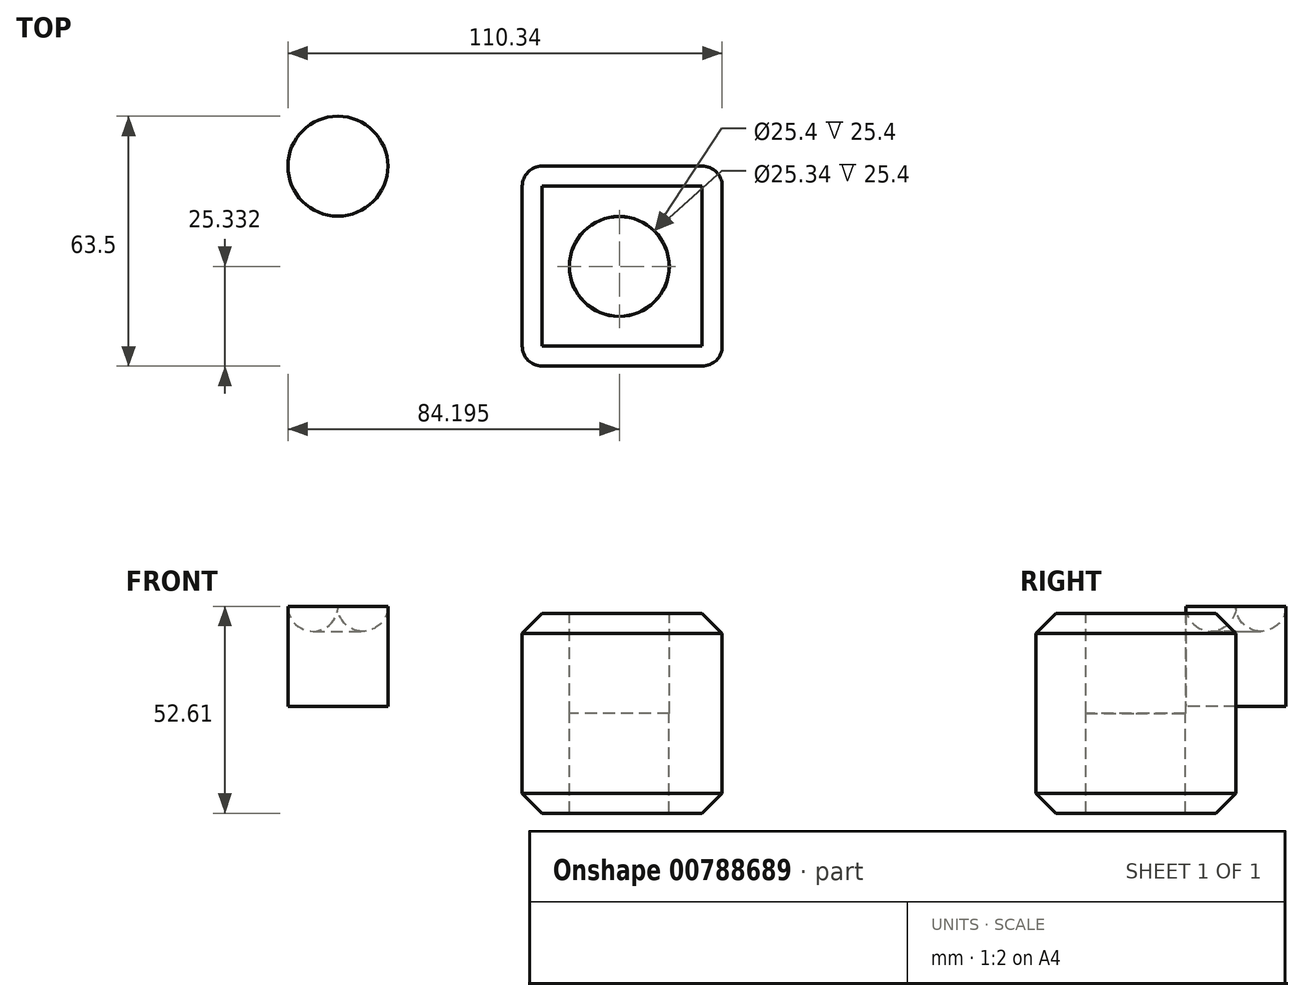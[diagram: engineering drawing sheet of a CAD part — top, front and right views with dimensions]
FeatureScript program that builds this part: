
annotation { "Feature Type Name" : "Feature", "Feature Type Description" : "" }
export const myFeature = defineFeature(function(context is Context, id is Id, definition is map)
    precondition{}
    {
        {
            var Q0;
            Q0=qCreatedBy(makeId("Front.planeOp"),FACE);
            var sketch = newSketch(context, id + "F0", { "sketchPlane" : qUnion([Q0])});
            skLineSegment(sketch, "E0", {"start": v(-40.12, 34.82) * mm, "end": v(-40.12, 9.42) * mm});
            skLineSegment(sketch, "E1", {"start": v(-40.12, 9.42) * mm, "end": v(-27.42, 9.42) * mm});
            skLineSegment(sketch, "E2", {"start": v(-27.42, 9.42) * mm, "end": v(-27.42, 35.24) * mm});
            skArc(sketch, "E3", {"start": v(-27.42, 35.24) * mm, "mid": v(-33.97, 41.17) * mm, "end": v(-40.12, 34.82) * mm});
            skSolve(sketch);
        }
        {
            var Q0;
            Q0 = qSketchRegion(id + "F0", true);
            var Q1;
            Q1=sQuery(id+"F0.wireOp",EDGE,"E2");
            revolve(context, id + "F1", {"surfaceOperationType" : NewSurfaceOperationType.NEW, "entities" : qUnion([Q0]), "axis" : qUnion([Q1]), "revolveType" : RevolveType.FULL});
        }
        {
            var Q0;
            Q0=qCreatedBy(makeId("Front.planeOp"),FACE);
            var sketch = newSketch(context, id + "F2", { "sketchPlane" : qUnion([Q0])});
            skLineSegment(sketch, "E4", {"start": v(19.42, 33) * mm, "end": v(19.42, -17.8) * mm});
            skLineSegment(sketch, "E5", {"start": v(19.42, -17.8) * mm, "end": v(70.22, -17.8) * mm});
            skLineSegment(sketch, "E6", {"start": v(70.22, -17.8) * mm, "end": v(70.22, 33) * mm});
            skLineSegment(sketch, "E7", {"start": v(70.22, 33) * mm, "end": v(19.42, 33) * mm});
            skSolve(sketch);
        }
        {
            var Q0;
            Q0 = qSketchRegion(id + "F2", true);
            extrude(context, id + "F3", {"entities" : qUnion([Q0]), "depth" : 50.8 * mm, "offsetDistance" : 25.4 * mm});
        }
        {
            var Q0;
            Q0=makeQuery(id+"F3.opExtrude","CAP_EDGE",EDGE,{"disambiguationData":[OSD([sQuery(id+"F2.wireOp",EDGE,"E4")])],"isStart":false});
            fillet(context, id + "F4", {"entities" : qUnion([Q0]), "radius" : 5.08 * mm, "tangentPropagation" : true, "allowEdgeOverflow" : false});
        }
        {
            var Q0;
            Q0=makeQuery(id+"F3.opExtrude","CAP_EDGE",EDGE,{"disambiguationData":[OSD([sQuery(id+"F2.wireOp",EDGE,"E6")])],"isStart":false});
            var Q1;
            Q1=makeQuery(id+"F3.opExtrude","CAP_EDGE",EDGE,{"disambiguationData":[OSD([sQuery(id+"F2.wireOp",EDGE,"E6")])],"isStart":true});
            fillet(context, id + "F5", {"entities" : qUnion([Q0, Q1]), "radius" : 5.08 * mm, "tangentPropagation" : true, "allowEdgeOverflow" : false});
        }
        {
            var Q0;
            Q0=makeQuery(id+"F3.opExtrude","CAP_EDGE",EDGE,{"disambiguationData":[OSD([sQuery(id+"F2.wireOp",EDGE,"E4")])],"isStart":true});
            fillet(context, id + "F6", {"entities" : qUnion([Q0]), "radius" : 5.08 * mm, "tangentPropagation" : true, "allowEdgeOverflow" : false});
        }
        {
            var Q0;
            Q0=makeQuery(id+"F3.opExtrude","SWEPT_FACE",FACE,{"disambiguationData":[OSD([sQuery(id+"F2.wireOp",EDGE,"E7")])]});
            chamfer(context, id + "F7", {"entities" : qUnion([Q0]), "width" : 5.08 * mm, "tangentPropagation" : true});
        }
        {
            var Q0;
            Q0=makeQuery(id+"F3.opExtrude","SWEPT_FACE",FACE,{"disambiguationData":[OSD([sQuery(id+"F2.wireOp",EDGE,"E5")])]});
            chamfer(context, id + "F8", {"entities" : qUnion([Q0]), "width" : 5.08 * mm, "tangentPropagation" : true});
        }
        {
            var Q0;
            Q0=makeQuery(id+"F3.opExtrude","SWEPT_FACE",FACE,{"disambiguationData":[OSD([sQuery(id+"F2.wireOp",EDGE,"E7")])]});
            var sketch = newSketch(context, id + "F9", { "sketchPlane" : qUnion([Q0])});
            skCircle(sketch, "E8", {"center": v(44.08, -25.47) * mm, "radius": 12.7 * mm});
            skSolve(sketch);
        }
        {
            var Q0;
            Q0=makeQuery(id+"F9.imprint","IMPRINT",FACE,{"disambiguationData":[TD([[makeQuery(id+"F9.imprint","IMPRINT",EDGE,{"derivedFrom":sQuery(id+"F9.wireOp",EDGE,"E8")}),1.0]])]});
            extrude(context, id + "F10", {"entities" : qUnion([Q0]), "operationType" : NewBodyOperationType.REMOVE, "oppositeDirection" : true, "depth" : 25.4 * mm, "offsetDistance" : 25.4 * mm});
        }
        {
            var Q0;
            Q0=makeQuery(id+"F10.boolean.opBoolean","COPY",FACE,{"derivedFrom":makeQuery(id+"F10.opExtrude","CAP_FACE",FACE,{"disambiguationData":[OSD([sQuery(id+"F9.wireOp",EDGE,"E8")])],"isStart":false})});
            var sketch = newSketch(context, id + "F11", { "sketchPlane" : qUnion([Q0])});
            skCircle(sketch, "E9", {"center": v(44.08, -25.47) * mm, "radius": 12.67 * mm});
            skSolve(sketch);
        }
        {
            var Q0;
            Q0 = qSketchRegion(id + "F11", true);
            extrude(context, id + "F12", {"entities" : qUnion([Q0]), "operationType" : NewBodyOperationType.REMOVE, "oppositeDirection" : true, "depth" : 25.4 * mm, "offsetDistance" : 25.4 * mm});
        }
    });
